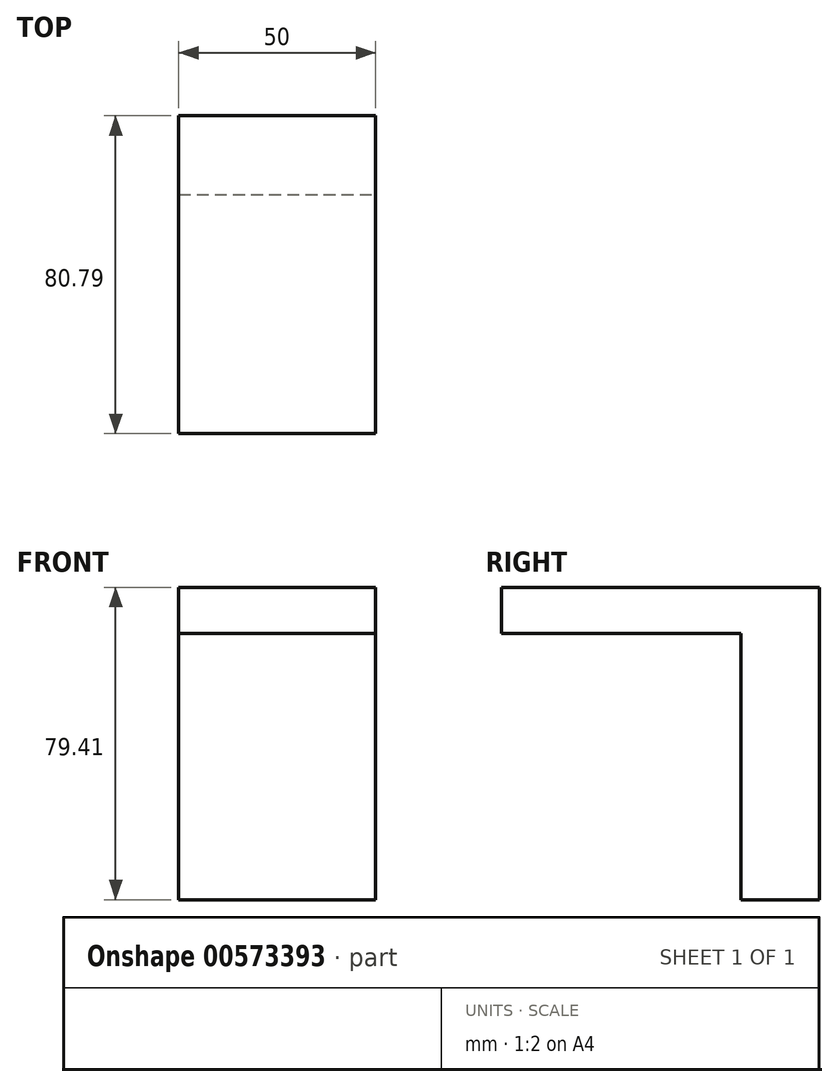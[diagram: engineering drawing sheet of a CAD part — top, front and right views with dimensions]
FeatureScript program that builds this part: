
annotation { "Feature Type Name" : "Feature", "Feature Type Description" : "" }
export const myFeature = defineFeature(function(context is Context, id is Id, definition is map)
    precondition{}
    {
        {
            var Q0;
            Q0=qCreatedBy(makeId("Top.planeOp"),FACE);
            var sketch = newSketch(context, id + "F0", { "sketchPlane" : qUnion([Q0])});
            skLineSegment(sketch, "E0.bottom", {"start": v(0, 0) * mm, "end": v(50, 0) * mm});
            skLineSegment(sketch, "E0.top", {"start": v(0, 20) * mm, "end": v(50, 20) * mm});
            skLineSegment(sketch, "E0.left", {"start": v(0, 0) * mm, "end": v(0, 20) * mm});
            skLineSegment(sketch, "E0.right", {"start": v(50, 0) * mm, "end": v(50, 20) * mm});
            skSolve(sketch);
        }
        {
            var Q0;
            Q0=makeQuery(id+"F0.imprint","IMPRINT",FACE,{"disambiguationData":[TD([[makeQuery(id+"F0.imprint","IMPRINT",EDGE,{"derivedFrom":sQuery(id+"F0.wireOp",EDGE,"E0.bottom")}),1.0]])]});
            var sketch = newSketch(context, id + "F1", { "sketchPlane" : qUnion([Q0])});
            skSolve(sketch);
        }
        {
            var Q0;
            Q0 = qSketchRegion(id + "F1", true);
            var Q1;
            Q1=makeQuery(id+"F1.imprint","IMPRINT",FACE,{"disambiguationData":[TD([[makeQuery(id+"F1.imprint","IMPRINT",EDGE,{"derivedFrom":makeQuery(id+"F0.imprint","IMPRINT",EDGE,{"derivedFrom":sQuery(id+"F0.wireOp",EDGE,"E0.bottom")})}),1.0]])]});
            extrude(context, id + "F2", {"entities" : qUnion([Q0, Q1]), "depth" : 79.4 * mm, "offsetDistance" : 25 * mm});
        }
        {
            var Q0;
            Q0=makeQuery(id+"F2.opExtrude","SWEPT_FACE",FACE,{"disambiguationData":[OSD([sQuery(id+"F0.wireOp",EDGE,"E0.bottom")])]});
            var sketch = newSketch(context, id + "F3", { "sketchPlane" : qUnion([Q0])});
            skLineSegment(sketch, "E1", {"start": v(0, 67.72) * mm, "end": v(50, 67.72) * mm});
            skSolve(sketch);
        }
        {
            var Q0;
            {var subQ0=sQuery(id+"F3.wireOp",EDGE,"E1");Q0=makeQuery(id+"F3.imprint","IMPRINT",FACE,{"disambiguationData":[TD([[makeQuery(id+"F3.imprint","IMPRINT",EDGE,{"derivedFrom":subQ0}),1.0]])]});}
            var sketch = newSketch(context, id + "F4", { "sketchPlane" : qUnion([Q0])});
            skSolve(sketch);
        }
        {
            var Q0;
            Q0 = qSketchRegion(id + "F4", true);
            var Q1;
            {var subQ0=sQuery(id+"F3.wireOp",EDGE,"E1");Q1=makeQuery(id+"F4.imprint","IMPRINT",FACE,{"disambiguationData":[TD([[makeQuery(id+"F4.imprint","IMPRINT",EDGE,{"derivedFrom":makeQuery(id+"F3.imprint","IMPRINT",EDGE,{"derivedFrom":subQ0})}),1.0]])]});}
            extrude(context, id + "F5", {"entities" : qUnion([Q0, Q1]), "operationType" : NewBodyOperationType.ADD, "depth" : 60.8 * mm, "offsetDistance" : 25 * mm});
        }
    });
